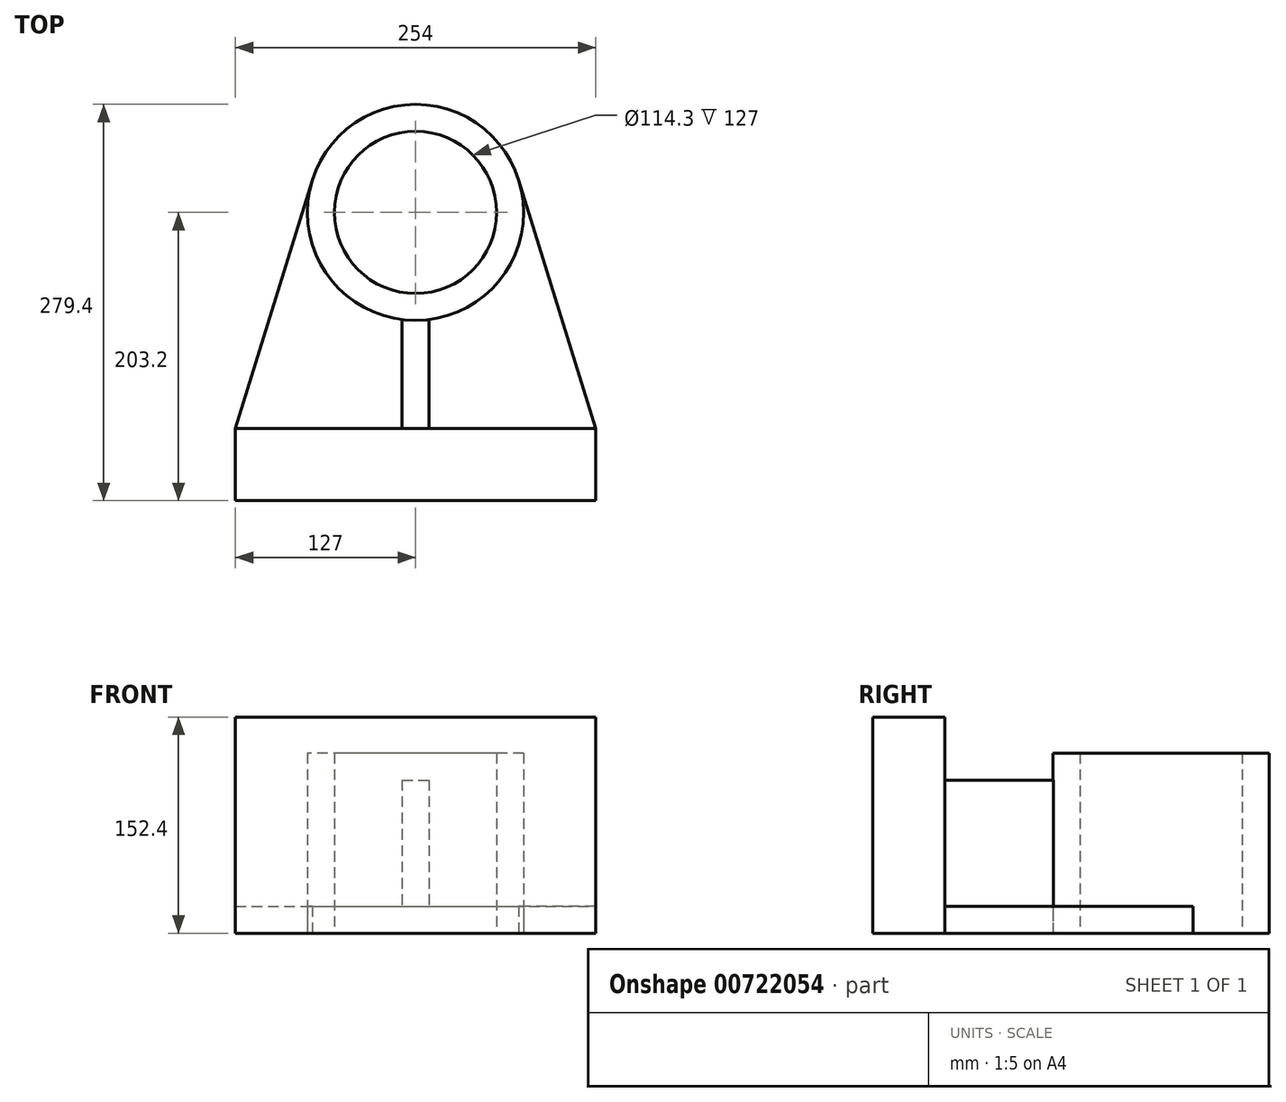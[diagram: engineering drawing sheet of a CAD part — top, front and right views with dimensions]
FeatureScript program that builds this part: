
annotation { "Feature Type Name" : "Feature", "Feature Type Description" : "" }
export const myFeature = defineFeature(function(context is Context, id is Id, definition is map)
    precondition{}
    {
        {
            var Q0;
            Q0=qCreatedBy(makeId("Top.planeOp"),FACE);
            var sketch = newSketch(context, id + "F0", { "sketchPlane" : qUnion([Q0])});
            skLineSegment(sketch, "E0.bottom", {"start": v(127, -25.4) * mm, "end": v(-127, -25.4) * mm});
            skLineSegment(sketch, "E0.top", {"start": v(127, 25.4) * mm, "end": v(-127, 25.4) * mm});
            skLineSegment(sketch, "E0.left", {"start": v(127, -25.4) * mm, "end": v(127, 25.4) * mm});
            skLineSegment(sketch, "E0.right", {"start": v(-127, -25.4) * mm, "end": v(-127, 25.4) * mm});
            skPoint(sketch, "E0.middle", {"position": v(0, 0) * mm});
            skSolve(sketch);
        }
        {
            var Q0;
            Q0 = qSketchRegion(id + "F0", true);
            extrude(context, id + "F1", {"entities" : qUnion([Q0]), "depth" : 152.4 * mm, "offsetDistance" : 25.4 * mm});
        }
        {
            var Q0;
            Q0=qCreatedBy(makeId("Top.planeOp"),FACE);
            var sketch = newSketch(context, id + "F2", { "sketchPlane" : qUnion([Q0])});
            skCircle(sketch, "E1", {"center": v(0, 177.8) * mm, "radius": 76.2 * mm});
            skCircle(sketch, "E2", {"center": v(0, 177.8) * mm, "radius": 57.15 * mm});
            skSolve(sketch);
        }
        {
            var Q0;
            Q0=makeQuery(id+"F2.imprint","IMPRINT",FACE,{"disambiguationData":[TD([[makeQuery(id+"F2.imprint","IMPRINT",EDGE,{"derivedFrom":sQuery(id+"F2.wireOp",EDGE,"E1")}),1.0]])]});
            extrude(context, id + "F3", {"entities" : qUnion([Q0]), "depth" : 127 * mm, "offsetDistance" : 25.4 * mm});
        }
        {
            var Q0;
            Q0=qCreatedBy(makeId("Top.planeOp"),FACE);
            var sketch = newSketch(context, id + "F4", { "sketchPlane" : qUnion([Q0])});
            skLineSegment(sketch, "E3", {"start": v(-127, 25.4) * mm, "end": v(127, 25.4) * mm});
            skLineSegment(sketch, "E4", {"start": v(127, 25.4) * mm, "end": v(72.79, 200.35) * mm});
            skLineSegment(sketch, "E5", {"start": v(-127, 25.4) * mm, "end": v(-72.79, 200.35) * mm});
            skArc(sketch, "E6", {"start": v(72.79, 200.35) * mm, "mid": v(0, 101.6) * mm, "end": v(-72.79, 200.35) * mm});
            skSolve(sketch);
        }
        {
            var Q0;
            Q0 = qSketchRegion(id + "F4", true);
            extrude(context, id + "F5", {"entities" : qUnion([Q0]), "depth" : 19.05 * mm, "offsetDistance" : 25.4 * mm});
        }
        {
            var Q0;
            Q0=makeQuery(id+"F5.opExtrude","CAP_FACE",FACE,{"disambiguationData":[OSD([sQuery(id+"F4.wireOp",EDGE,"E3"),sQuery(id+"F4.wireOp",EDGE,"E4"),sQuery(id+"F4.wireOp",EDGE,"E5"),sQuery(id+"F4.wireOp",EDGE,"E6")])],"isStart":false});
            var sketch = newSketch(context, id + "F6", { "sketchPlane" : qUnion([Q0])});
            skLineSegment(sketch, "E7", {"start": v(9.53, 102.2) * mm, "end": v(9.53, 25.4) * mm});
            skLineSegment(sketch, "E8", {"start": v(9.53, 25.4) * mm, "end": v(-9.52, 25.4) * mm});
            skLineSegment(sketch, "E9", {"start": v(-9.52, 25.4) * mm, "end": v(-9.52, 102.2) * mm});
            skArc(sketch, "E10", {"start": v(-9.52, 102.2) * mm, "mid": v(0, 101.6) * mm, "end": v(9.53, 102.2) * mm});
            skLineSegment(sketch, "E11", {"start": v(-9.52, 25.4) * mm, "end": v(9.53, 25.4) * mm});
            skSolve(sketch);
        }
        {
            var Q0;
            Q0 = qSketchRegion(id + "F6", true);
            extrude(context, id + "F7", {"entities" : qUnion([Q0]), "depth" : 88.9 * mm, "offsetDistance" : 25.4 * mm});
        }
    });
